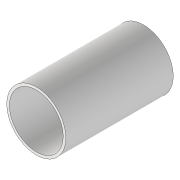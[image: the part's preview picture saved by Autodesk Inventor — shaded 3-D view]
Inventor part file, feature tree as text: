
AUTODESK INVENTOR PART (.ipt)
format: ipt  version: 2020 (Build 240168000, 168)  size: 87,040 bytes
history: native  units: mm
features: extrude x1, sketch x1
ambient origin geometry x8: Origin, YZ Plane, XZ Plane, XY Plane, X Axis, Y Axis, Z Axis, Center Point
bodies: Volumenkörper1 (feature_tree)
feature tree (2):
  extrude  "Extrusion1"  Depth=200.0mm
  sketch  "Skizze1"  dims[d0=100.0mm d1=110.0mm d2=200.0mm d3=0.0mm]
